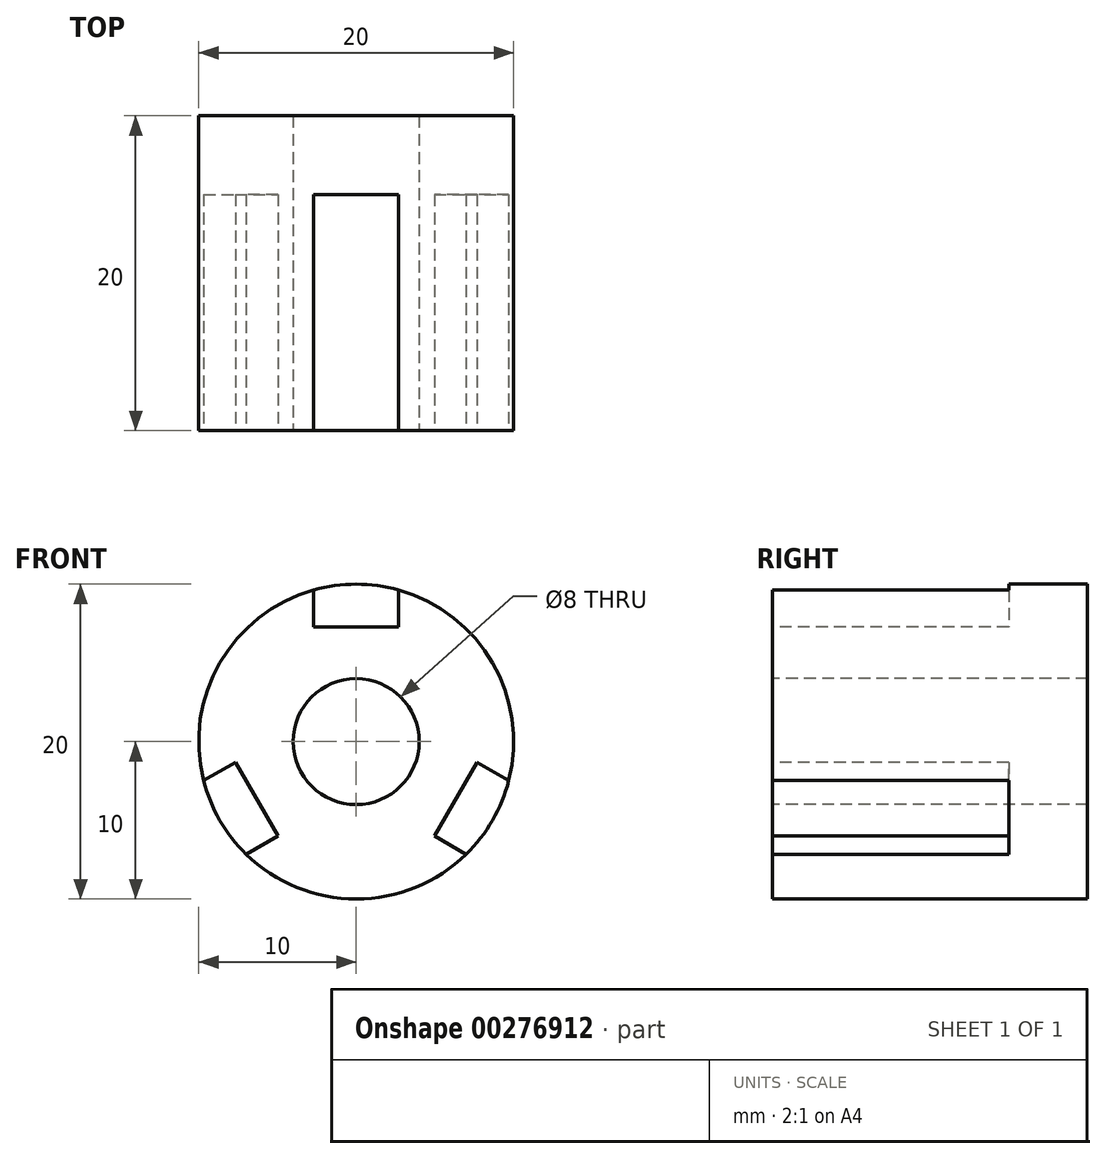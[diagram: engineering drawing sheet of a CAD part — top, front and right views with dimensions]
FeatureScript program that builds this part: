
annotation { "Feature Type Name" : "Feature", "Feature Type Description" : "" }
export const myFeature = defineFeature(function(context is Context, id is Id, definition is map)
    precondition{}
    {
        {
            var Q0;
            Q0=qCreatedBy(makeId("Front.planeOp"),FACE);
            var sketch = newSketch(context, id + "F0", { "sketchPlane" : qUnion([Q0])});
            skCircle(sketch, "E0", {"center": v(0, 0) * mm, "radius": 10 * mm});
            skCircle(sketch, "E1", {"center": v(0, 0) * mm, "radius": 4 * mm});
            skCircle(sketch, "E2", {"center": v(0, 0) * mm, "radius": 7.3 * mm, "construction": true});
            skLineSegment(sketch, "E3", {"start": v(0, 0) * mm, "end": v(0, 10) * mm, "construction": true});
            skLineSegment(sketch, "E4", {"start": v(-2.7, 9.63) * mm, "end": v(-2.7, 7.3) * mm});
            skLineSegment(sketch, "E5", {"start": v(-2.7, 7.3) * mm, "end": v(2.7, 7.3) * mm});
            skLineSegment(sketch, "E6", {"start": v(2.7, 7.3) * mm, "end": v(2.7, 9.63) * mm});
            skLineSegment(sketch, "E7", {"start": v(9.69, -2.48) * mm, "end": v(7.67, -1.31) * mm});
            skLineSegment(sketch, "E8", {"start": v(7.67, -1.31) * mm, "end": v(4.97, -5.99) * mm});
            skLineSegment(sketch, "E9", {"start": v(4.97, -5.99) * mm, "end": v(6.99, -7.15) * mm});
            skLineSegment(sketch, "E10", {"start": v(0, 0) * mm, "end": v(8.66, 5) * mm, "construction": true});
            skLineSegment(sketch, "E11", {"start": v(0, 0) * mm, "end": v(-8.66, 5) * mm, "construction": true});
            skLineSegment(sketch, "E12", {"start": v(-9.69, -2.48) * mm, "end": v(-7.67, -1.31) * mm});
            skLineSegment(sketch, "E13", {"start": v(-7.67, -1.31) * mm, "end": v(-4.97, -5.99) * mm});
            skLineSegment(sketch, "E14", {"start": v(-4.97, -5.99) * mm, "end": v(-6.99, -7.15) * mm});
            skSolve(sketch);
        }
        {
            var Q0;
            Q0=makeQuery(id+"F0.imprint","IMPRINT",FACE,{"disambiguationData":[TD([[makeQuery(id+"F0.imprint","IMPRINT",EDGE,{"derivedFrom":sQuery(id+"F0.wireOp",EDGE,"E1")}),-1.0]])]});
            var Q1;
            {var subQ0=sQuery(id+"F0.wireOp",EDGE,"E12");Q1=makeQuery(id+"F0.imprint","IMPRINT",FACE,{"disambiguationData":[TD([[makeQuery(id+"F0.imprint","IMPRINT",EDGE,{"derivedFrom":subQ0}),-1.0]])]});}
            var Q2;
            {var subQ0=sQuery(id+"F0.wireOp",EDGE,"E4");Q2=makeQuery(id+"F0.imprint","IMPRINT",FACE,{"disambiguationData":[TD([[makeQuery(id+"F0.imprint","IMPRINT",EDGE,{"derivedFrom":subQ0}),1.0]])]});}
            var Q3;
            {var subQ0=sQuery(id+"F0.wireOp",EDGE,"E7");Q3=makeQuery(id+"F0.imprint","IMPRINT",FACE,{"disambiguationData":[TD([[makeQuery(id+"F0.imprint","IMPRINT",EDGE,{"derivedFrom":subQ0}),1.0]])]});}
            extrude(context, id + "F1", {"entities" : qUnion([Q0, Q1, Q2, Q3]), "oppositeDirection" : true, "depth" : 20 * mm});
        }
        {
            var Q0;
            {var subQ0=sQuery(id+"F0.wireOp",EDGE,"E12");Q0=makeQuery(id+"F0.imprint","IMPRINT",FACE,{"disambiguationData":[TD([[makeQuery(id+"F0.imprint","IMPRINT",EDGE,{"derivedFrom":subQ0}),-1.0]])]});}
            var Q1;
            {var subQ0=sQuery(id+"F0.wireOp",EDGE,"E4");Q1=makeQuery(id+"F0.imprint","IMPRINT",FACE,{"disambiguationData":[TD([[makeQuery(id+"F0.imprint","IMPRINT",EDGE,{"derivedFrom":subQ0}),1.0]])]});}
            var Q2;
            {var subQ0=sQuery(id+"F0.wireOp",EDGE,"E7");Q2=makeQuery(id+"F0.imprint","IMPRINT",FACE,{"disambiguationData":[TD([[makeQuery(id+"F0.imprint","IMPRINT",EDGE,{"derivedFrom":subQ0}),1.0]])]});}
            extrude(context, id + "F2", {"entities" : qUnion([Q0, Q1, Q2]), "operationType" : NewBodyOperationType.REMOVE, "oppositeDirection" : true, "depth" : 15 * mm});
        }
    });
